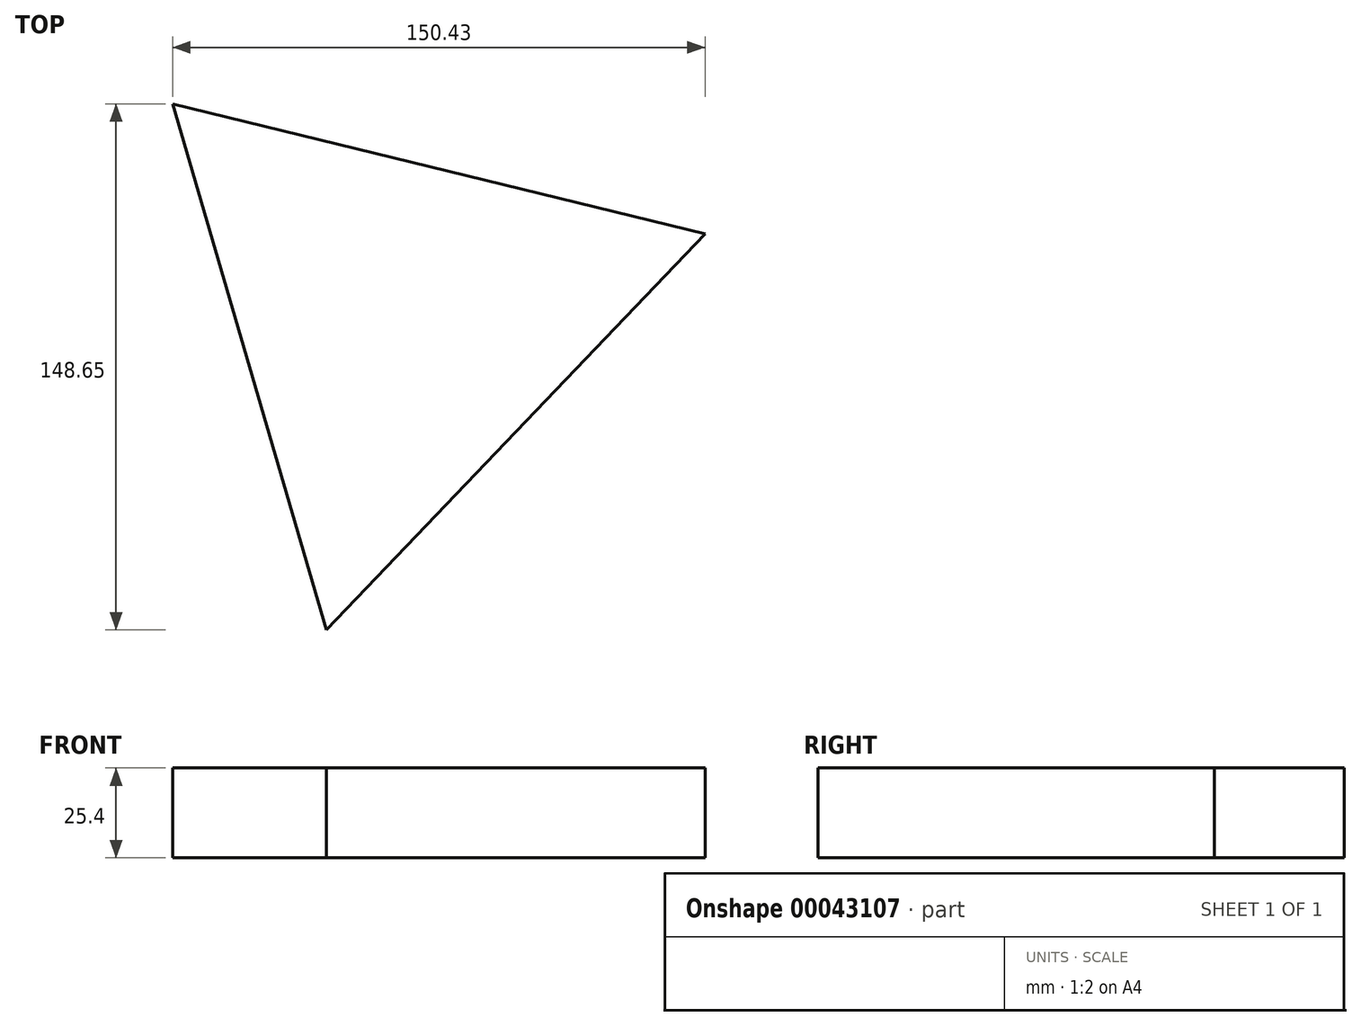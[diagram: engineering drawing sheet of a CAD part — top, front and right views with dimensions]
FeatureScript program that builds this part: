
annotation { "Feature Type Name" : "Feature", "Feature Type Description" : "" }
export const myFeature = defineFeature(function(context is Context, id is Id, definition is map)
    precondition{}
    {
        {
            var Q0;
            Q0=qCreatedBy(makeId("Top.planeOp"),FACE);
            var sketch = newSketch(context, id + "F0", { "sketchPlane" : qUnion([Q0])});
            skCircle(sketch, "E0.cCircle", {"center": v(0, 0) * mm, "radius": 44.7 * mm, "construction": true});
            skLineSegment(sketch, "E0.0", {"start": v(-64.6, 61.8) * mm, "end": v(85.82, 25.05) * mm});
            skLineSegment(sketch, "E0.1", {"start": v(85.82, 25.05) * mm, "end": v(-21.22, -86.85) * mm});
            skLineSegment(sketch, "E0.2", {"start": v(-21.22, -86.85) * mm, "end": v(-64.6, 61.8) * mm});
            skPoint(sketch, "E0.0.midPoint", {"position": v(10.6, 43.43) * mm});
            skSolve(sketch);
        }
        {
            var Q0;
            Q0 = qSketchRegion(id + "F0", true);
            extrude(context, id + "F1", {"entities" : qUnion([Q0]), "depth" : 25.4 * mm});
        }
        {
            var Q0;
            Q0=makeQuery(id+"F1.opExtrude","CAP_FACE",FACE,{"disambiguationData":[OSD([sQuery(id+"F0.wireOp",EDGE,"E0.0"),sQuery(id+"F0.wireOp",EDGE,"E0.1"),sQuery(id+"F0.wireOp",EDGE,"E0.2")])],"isStart":false});
            var sketch = newSketch(context, id + "F2", { "sketchPlane" : qUnion([Q0])});
            skPoint(sketch, "E1", {"position": v(10.6, 43.43) * mm});
            skPoint(sketch, "E2", {"position": v(32.3, -30.9) * mm});
            skPoint(sketch, "E3", {"position": v(-42.91, -12.53) * mm});
            skLineSegment(sketch, "E4", {"start": v(10.6, 43.43) * mm, "end": v(-42.91, -12.53) * mm});
            skLineSegment(sketch, "E5", {"start": v(32.3, -30.9) * mm, "end": v(10.6, 43.43) * mm});
            skLineSegment(sketch, "E6", {"start": v(-42.91, -12.53) * mm, "end": v(32.3, -30.9) * mm});
            skSolve(sketch);
        }
        {
            var Q0;
            Q0=makeQuery(id+"F2.imprint","IMPRINT",FACE,{"disambiguationData":[TD([[makeQuery(id+"F2.imprint","IMPRINT",EDGE,{"derivedFrom":sQuery(id+"F2.wireOp",EDGE,"E4")}),1.0]])]});
            extrude(context, id + "F3", {"entities" : qUnion([Q0]), "operationType" : NewBodyOperationType.REMOVE, "depth" : 1.27 * mm});
        }
    });
